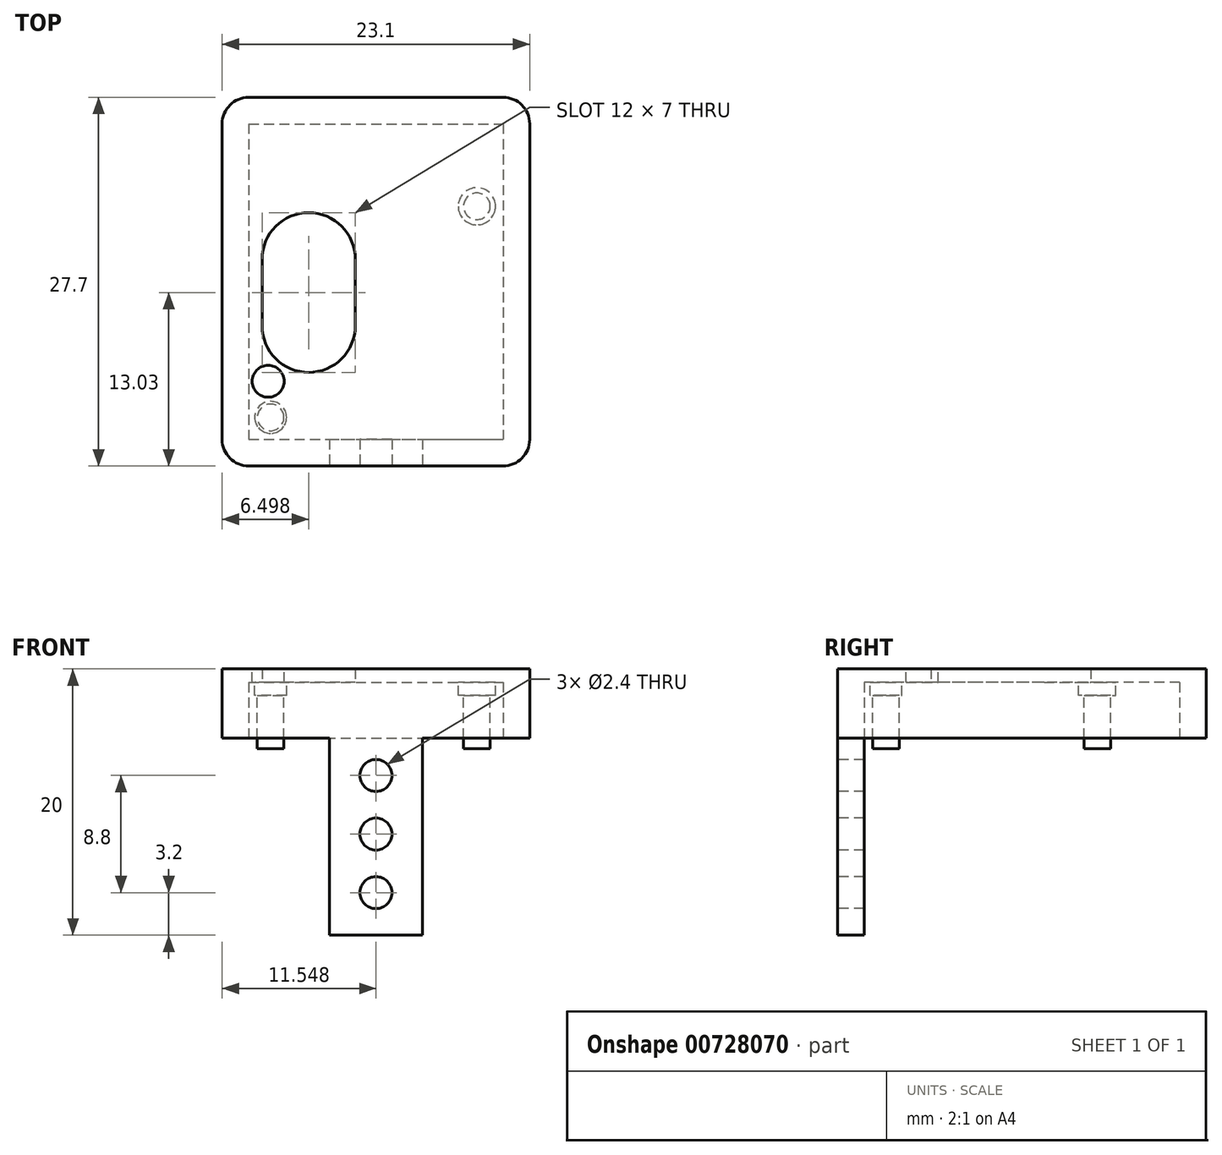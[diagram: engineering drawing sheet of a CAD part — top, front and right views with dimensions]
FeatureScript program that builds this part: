
annotation { "Feature Type Name" : "Feature", "Feature Type Description" : "" }
export const myFeature = defineFeature(function(context is Context, id is Id, definition is map)
    precondition{}
    {
        {
            var Q0;
            Q0=qCreatedBy(makeId("Top.planeOp"),FACE);
            var sketch = newSketch(context, id + "F0", { "sketchPlane" : qUnion([Q0])});
            skLineSegment(sketch, "E0.bottom", {"start": v(-11.62, 23.7) * mm, "end": v(7.48, 23.7) * mm, "construction": true});
            skLineSegment(sketch, "E0.top", {"start": v(-11.62, 0) * mm, "end": v(7.48, 0) * mm, "construction": true});
            skLineSegment(sketch, "E0.left", {"start": v(-11.62, 23.7) * mm, "end": v(-11.62, 0) * mm, "construction": true});
            skLineSegment(sketch, "E0.right", {"start": v(7.48, 23.7) * mm, "end": v(7.48, 0) * mm, "construction": true});
            skLineSegment(sketch, "E1.bottom", {"start": v(-7.12, 17.03) * mm, "end": v(-7.12, 17.03) * mm});
            skLineSegment(sketch, "E1.top", {"start": v(-7.12, 5.03) * mm, "end": v(-7.12, 5.03) * mm});
            skLineSegment(sketch, "E1.left", {"start": v(-10.62, 13.53) * mm, "end": v(-10.62, 8.53) * mm});
            skLineSegment(sketch, "E1.right", {"start": v(-3.62, 13.53) * mm, "end": v(-3.62, 8.53) * mm});
            skPoint(sketch, "E2.visualSharp", {"position": v(-10.62, 17.03) * mm});
            skArc(sketch, "E2.filletArc", {"start": v(-7.12, 17.03) * mm, "mid": v(-9.6, 16) * mm, "end": v(-10.62, 13.53) * mm});
            skPoint(sketch, "E3.visualSharp", {"position": v(-3.62, 17.03) * mm});
            skArc(sketch, "E3.filletArc", {"start": v(-3.62, 13.53) * mm, "mid": v(-4.65, 16) * mm, "end": v(-7.12, 17.03) * mm});
            skPoint(sketch, "E4.visualSharp", {"position": v(-10.62, 5.03) * mm});
            skArc(sketch, "E4.filletArc", {"start": v(-10.62, 8.53) * mm, "mid": v(-9.6, 6.06) * mm, "end": v(-7.12, 5.03) * mm});
            skPoint(sketch, "E5.visualSharp", {"position": v(-3.62, 5.03) * mm});
            skArc(sketch, "E5.filletArc", {"start": v(-7.12, 5.03) * mm, "mid": v(-4.65, 6.06) * mm, "end": v(-3.62, 8.53) * mm});
            skLineSegment(sketch, "E6", {"start": v(-30.2, 11.03) * mm, "end": v(-3.62, 11.03) * mm, "construction": true});
            skLineSegment(sketch, "E7.bottom", {"start": v(-13.62, 25.7) * mm, "end": v(9.48, 25.7) * mm});
            skLineSegment(sketch, "E7.top", {"start": v(-13.62, -2) * mm, "end": v(9.48, -2) * mm});
            skLineSegment(sketch, "E7.left", {"start": v(-13.62, 25.7) * mm, "end": v(-13.62, -2) * mm});
            skLineSegment(sketch, "E7.right", {"start": v(9.48, 25.7) * mm, "end": v(9.48, -2) * mm});
            skSolve(sketch);
        }
        {
            var Q0;
            Q0=makeQuery(id+"F0.imprint","IMPRINT",FACE,{"disambiguationData":[TD([[makeQuery(id+"F0.imprint","IMPRINT",EDGE,{"derivedFrom":sQuery(id+"F0.wireOp",EDGE,"E1.left")}),-1.0]])]});
            var Q1;
            Q1 = qSketchRegion(id + "F0", true);
            extrude(context, id + "F1", {"entities" : qUnion([Q0, Q1]), "depth" : 5.2 * mm, "offsetDistance" : 25 * mm});
        }
        {
            var Q0;
            Q0=qCreatedBy(makeId("Top.planeOp"),FACE);
            var sketch = newSketch(context, id + "F2", { "sketchPlane" : qUnion([Q0])});
            skLineSegment(sketch, "E8.bottom", {"start": v(-11.62, 23.7) * mm, "end": v(7.48, 23.7) * mm});
            skLineSegment(sketch, "E8.top", {"start": v(-11.62, 0) * mm, "end": v(7.48, 0) * mm});
            skLineSegment(sketch, "E8.left", {"start": v(-11.62, 23.7) * mm, "end": v(-11.62, 0) * mm});
            skLineSegment(sketch, "E8.right", {"start": v(7.48, 23.7) * mm, "end": v(7.48, 0) * mm});
            skSolve(sketch);
        }
        {
            var Q0;
            Q0 = qSketchRegion(id + "F2", true);
            extrude(context, id + "F3", {"entities" : qUnion([Q0]), "operationType" : NewBodyOperationType.REMOVE, "depth" : 4.2 * mm, "offsetDistance" : 25 * mm});
        }
        {
            var Q0;
            Q0=makeQuery(id+"F3.boolean.opBoolean","COPY",FACE,{"derivedFrom":makeQuery(id+"F3.opExtrude","CAP_FACE",FACE,{"disambiguationData":[OSD([sQuery(id+"F2.wireOp",EDGE,"E8.bottom"),sQuery(id+"F2.wireOp",EDGE,"E8.top"),sQuery(id+"F2.wireOp",EDGE,"E8.left"),sQuery(id+"F2.wireOp",EDGE,"E8.right")])],"isStart":false})});
            var sketch = newSketch(context, id + "F4", { "sketchPlane" : qUnion([Q0])});
            skCircle(sketch, "E9", {"center": v(5.5, -17.5) * mm, "radius": 1.4 * mm});
            skCircle(sketch, "E10", {"center": v(-9.98, -1.65) * mm, "radius": 1.2 * mm});
            skSolve(sketch);
        }
        {
            var Q0;
            Q0 = qSketchRegion(id + "F4", true);
            extrude(context, id + "F5", {"entities" : qUnion([Q0]), "operationType" : NewBodyOperationType.ADD, "depth" : 1 * mm, "offsetDistance" : 25 * mm});
        }
        {
            var Q0;
            Q0=makeQuery(id+"F5.opExtrude","CAP_FACE",FACE,{"disambiguationData":[OSD([sQuery(id+"F4.wireOp",EDGE,"E10")])],"isStart":false});
            var sketch = newSketch(context, id + "F6", { "sketchPlane" : qUnion([Q0])});
            skCircle(sketch, "E11", {"center": v(-9.98, -1.65) * mm, "radius": 1 * mm});
            skCircle(sketch, "E12", {"center": v(5.5, -17.5) * mm, "radius": 1 * mm});
            skSolve(sketch);
        }
        {
            var Q0;
            Q0 = qSketchRegion(id + "F6", true);
            extrude(context, id + "F7", {"entities" : qUnion([Q0]), "operationType" : NewBodyOperationType.ADD, "depth" : 4 * mm, "offsetDistance" : 25 * mm});
        }
        {
            var Q0;
            Q0=makeQuery(id+"F1.opExtrude","CAP_FACE",FACE,{"disambiguationData":[OSD([sQuery(id+"F0.wireOp",EDGE,"E1.left"),sQuery(id+"F0.wireOp",EDGE,"E1.right"),sQuery(id+"F0.wireOp",EDGE,"E2.filletArc"),sQuery(id+"F0.wireOp",EDGE,"E3.filletArc"),sQuery(id+"F0.wireOp",EDGE,"E4.filletArc"),sQuery(id+"F0.wireOp",EDGE,"E5.filletArc"),sQuery(id+"F0.wireOp",EDGE,"E7.bottom"),sQuery(id+"F0.wireOp",EDGE,"E7.top"),sQuery(id+"F0.wireOp",EDGE,"E7.left"),sQuery(id+"F0.wireOp",EDGE,"E7.right")])],"isStart":false});
            var sketch = newSketch(context, id + "F8", { "sketchPlane" : qUnion([Q0])});
            skCircle(sketch, "E13", {"center": v(-10.17, 4.36) * mm, "radius": 1.2 * mm});
            skSolve(sketch);
        }
        {
            var Q0;
            Q0=makeQuery(id+"F8.imprint","IMPRINT",FACE,{"disambiguationData":[TD([[makeQuery(id+"F8.imprint","IMPRINT",EDGE,{"derivedFrom":sQuery(id+"F8.wireOp",EDGE,"E13")}),-1.0]])]});
            var Q1;
            Q1=sQuery(id+"F8.wireOp",EDGE,"E13");
            extrude(context, id + "F9", {"entities" : qUnion([Q0]), "operationType" : NewBodyOperationType.INTERSECT, "surfaceEntities" : qUnion([Q1]), "endBound" : BoundingType.THROUGH_ALL, "oppositeDirection" : true, "depth" : 25 * mm, "offsetDistance" : 25 * mm});
        }
        {
            var Q0;
            Q0=makeQuery(id+"F1.opExtrude","SWEPT_EDGE",EDGE,{"disambiguationData":[OSD([sQuery(id+"F0.wireOp",EDGE,"E7.bottom"),sQuery(id+"F0.wireOp",EDGE,"E7.left")])]});
            var Q1;
            Q1=makeQuery(id+"F1.opExtrude","SWEPT_EDGE",EDGE,{"disambiguationData":[OSD([sQuery(id+"F0.wireOp",EDGE,"E7.top"),sQuery(id+"F0.wireOp",EDGE,"E7.left")])]});
            var Q2;
            Q2=makeQuery(id+"F1.opExtrude","SWEPT_EDGE",EDGE,{"disambiguationData":[OSD([sQuery(id+"F0.wireOp",EDGE,"E7.top"),sQuery(id+"F0.wireOp",EDGE,"E7.right")])]});
            var Q3;
            Q3=makeQuery(id+"F1.opExtrude","SWEPT_EDGE",EDGE,{"disambiguationData":[OSD([sQuery(id+"F0.wireOp",EDGE,"E7.bottom"),sQuery(id+"F0.wireOp",EDGE,"E7.right")])]});
            fillet(context, id + "F10", {"entities" : qUnion([Q0, Q1, Q2, Q3]), "radius" : 2 * mm, "tangentPropagation" : true, "allowEdgeOverflow" : false});
        }
        {
            var Q0;
            Q0=makeQuery(id+"F1.opExtrude","SWEPT_FACE",FACE,{"disambiguationData":[OSD([sQuery(id+"F0.wireOp",EDGE,"E7.top")])]});
            var sketch = newSketch(context, id + "F11", { "sketchPlane" : qUnion([Q0])});
            skLineSegment(sketch, "E14.bottom", {"start": v(-5.57, 5.2) * mm, "end": v(1.43, 5.2) * mm});
            skLineSegment(sketch, "E14.top", {"start": v(-5.57, -14.8) * mm, "end": v(1.43, -14.8) * mm});
            skLineSegment(sketch, "E14.left", {"start": v(-5.57, 5.2) * mm, "end": v(-5.57, -14.8) * mm});
            skLineSegment(sketch, "E14.right", {"start": v(1.43, 5.2) * mm, "end": v(1.43, -14.8) * mm});
            skCircle(sketch, "E15", {"center": v(-2.07, -2.8) * mm, "radius": 1.2 * mm});
            skLineSegment(sketch, "E16", {"start": v(-2.07, 10.18) * mm, "end": v(-2.07, -14.8) * mm, "construction": true});
            skCircle(sketch, "E17", {"center": v(-2.07, -7.2) * mm, "radius": 1.2 * mm});
            skCircle(sketch, "E18", {"center": v(-2.07, -11.6) * mm, "radius": 1.2 * mm});
            skSolve(sketch);
        }
        {
            var Q0;
            Q0 = qSketchRegion(id + "F11", true);
            extrude(context, id + "F12", {"entities" : qUnion([Q0]), "operationType" : NewBodyOperationType.ADD, "oppositeDirection" : true, "depth" : 2 * mm, "offsetDistance" : 25 * mm});
        }
    });
